# Revit family: MD2-AL4
name_source: partatom
category: Lighting Fixtures
units: mm (PartAtom-declared; Revit-internal decimal feet)

## family parameters
Always vertical = Yes
Cut with Voids When Loaded = No
Host = Ceiling
Light Source = Yes
Maintain Annotation Orientation = No
OmniClass Number = 23.80.70.11.14.11
OmniClass Title = Downlights
Part Type = Normal
Room Calculation Point = No
Round Connector Dimension = Use Diameter
Shared = No

## types (5) — shared parameters
Assembly Code = D5020200
Color Filter = 16777215
Default Elevation = 0' - 0"
Description = LED Recessed Medical Patient Ambient Exam Troffer
Dimming Lamp Color Temperature Shift = <None>
Emit from Line Length = 3' - 11 11/16"
Housing Finish = Metal - Viscor - White
Lamp = LED
Length = 3' - 11 11/16"
Lens Finsih = Polycarbonate - Viscor - Frosted
Manufacturer = CERTOLUX by VISCOR
Model = MD2-AL4
Tilt Angle = 90.00°
URL = https://www.viscor.com
Voltage = 120 V
Width = 0' - 3 3/4"

## per-type parameters (varying)
| type | Apparent Load | Lamp Wattage | Photometric Web File |
| MD2AL4-48-LED840K035LUNV (Ambient Mode) | 29 VA | 29 VA | MD2AL4-48-LED840K035LUNV (Ambient Mode).ies |
| MD2AL4-48-LED840K040LUNV (Ambient Mode) | 34 VA | 34 VA | MD2AL4-48-LED840K040LUNV (Ambient Mode).ies |
| MD2AL4-48-LED840K045LUNV (Ambient Mode) | 38 VA | 38 VA | MD2AL4-48-LED840K045LUNV (Ambient Mode).ies |
| MD2AL4-48-LED840K045L_024LUNV (Exam Mode) | 59 VA | 59 VA | MD2AL4-48-LED840K045L_024LUNV (Exam Mode).ies |
| MD2AL4-48-LED840K045L_028LUNV (Exam Mode) | 63 VA | 63 VA | MD2AL4-48-LED840K045L_028LUNV (Exam Mode).ies |

## geometry (parser evidence)
native form markers: Sweep x3
no freeform markers — native parametric forms only
